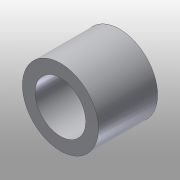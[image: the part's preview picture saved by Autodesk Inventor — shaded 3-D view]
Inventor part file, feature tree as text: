
AUTODESK INVENTOR PART (.ipt)
format: ipt  version: 2015 (Build 190159000, 159)  size: 87,552 bytes
history: native  units: mm
features: other x3, sketch x1
ambient origin geometry x8: Origin, YZ Plane, XZ Plane, XY Plane, X Axis, Y Axis, Z Axis, Center Point
bodies: Solid1 (feature_tree)
feature tree (4):
  other  "500-111.ipt"
  other  "Solid1::500-111.ipt"
  other  "TaggingFeature1"
  sketch  "Sketch1"  dims[d0=10.0mm]
